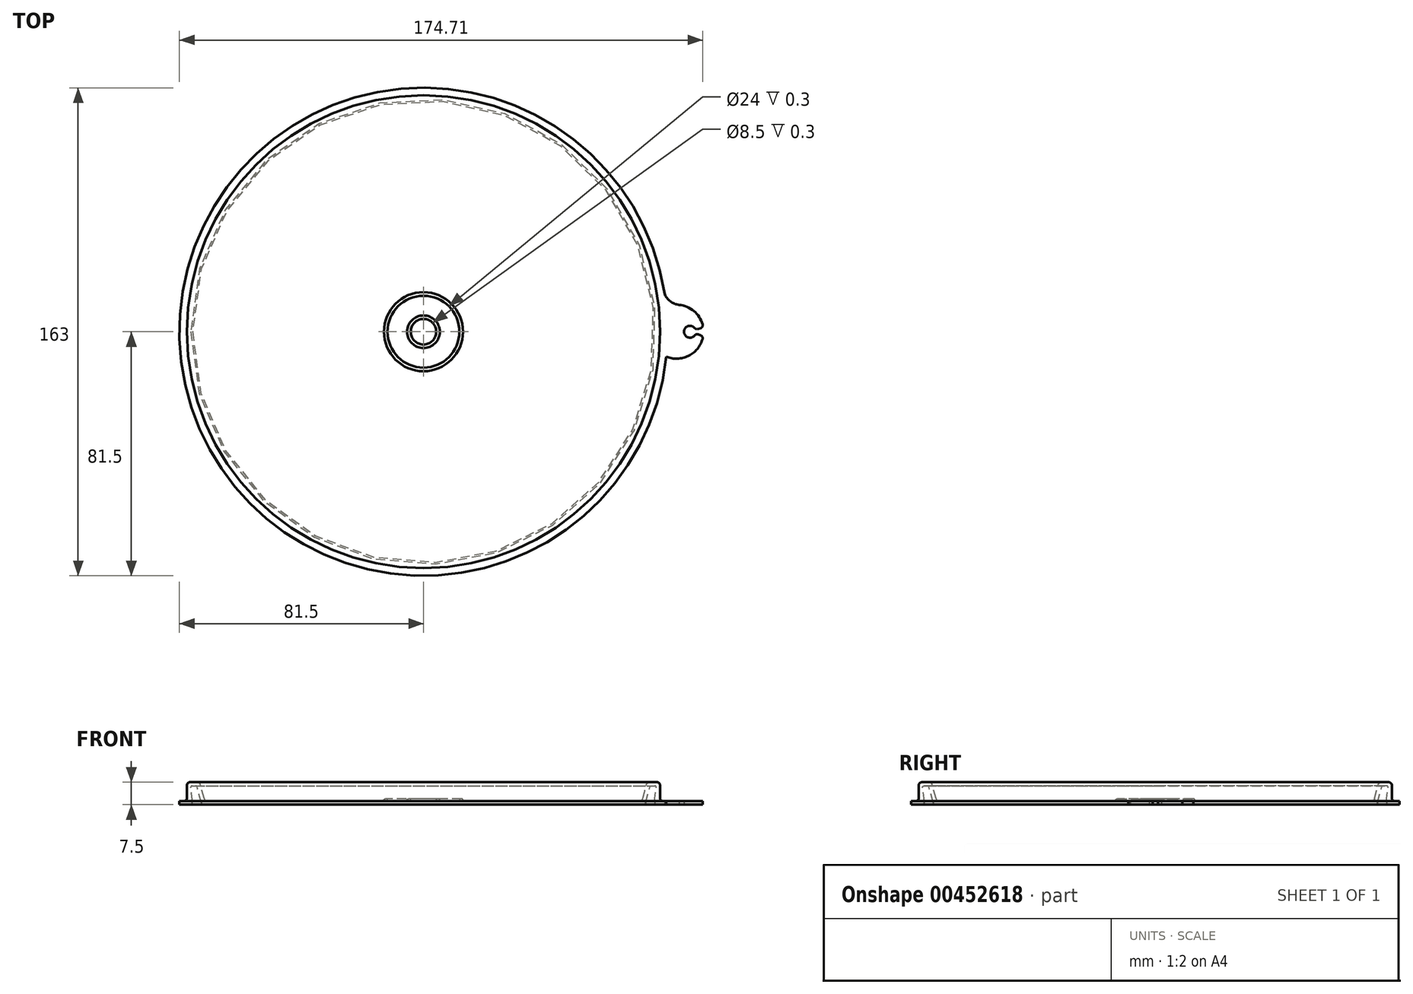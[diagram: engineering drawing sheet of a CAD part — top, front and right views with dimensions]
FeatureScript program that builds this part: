
annotation { "Feature Type Name" : "Feature", "Feature Type Description" : "" }
export const myFeature = defineFeature(function(context is Context, id is Id, definition is map)
    precondition{}
    {
        {
            var Q0;
            Q0=qCreatedBy(makeId("Top.planeOp"),FACE);
            var sketch = newSketch(context, id + "F0", { "sketchPlane" : qUnion([Q0]), "disableImprinting" : false});
            skCircle(sketch, "E0", {"center": v(0, 0) * mm, "radius": 73 * mm});
            skPoint(sketch, "E1", {"position": v(73, 0) * mm});
            skCircle(sketch, "E2", {"center": v(0, 0) * mm, "radius": 78 * mm, "construction": true});
            skLineSegment(sketch, "E3", {"start": v(0, 0) * mm, "end": v(76.56, 0) * mm, "construction": true});
            skSolve(sketch);
        }
        {
            var Q0;
            Q0 = qSketchRegion(id + "F0", true);
            extrude(context, id + "F1", {"entities" : qUnion([Q0]), "depth" : 1.2 * mm});
        }
        {
            var Q0;
            Q0=qCreatedBy(makeId("Front.planeOp"),FACE);
            var sketch = newSketch(context, id + "F2", { "sketchPlane" : qUnion([Q0]), "disableImprinting" : false});
            skLineSegment(sketch, "E4", {"start": v(73, 0) * mm, "end": v(73.23, 0) * mm});
            skLineSegment(sketch, "E5", {"start": v(74.2, 0.74) * mm, "end": v(75.59, 5.93) * mm});
            skLineSegment(sketch, "E6", {"start": v(76.07, 6.3) * mm, "end": v(77.2, 6.3) * mm});
            skLineSegment(sketch, "E7", {"start": v(77.7, 5.74) * mm, "end": v(77.14, 1.12) * mm});
            skLineSegment(sketch, "E8", {"start": v(78.13, 0) * mm, "end": v(81.5, 0) * mm});
            skLineSegment(sketch, "E9", {"start": v(81.5, 0) * mm, "end": v(81.5, 1.2) * mm});
            skLineSegment(sketch, "E10", {"start": v(81.5, 1.2) * mm, "end": v(79.97, 1.2) * mm});
            skLineSegment(sketch, "E11", {"start": v(78.97, 2.2) * mm, "end": v(78.97, 6.5) * mm});
            skLineSegment(sketch, "E12", {"start": v(77.97, 7.5) * mm, "end": v(75.46, 7.5) * mm});
            skLineSegment(sketch, "E13", {"start": v(74.49, 6.76) * mm, "end": v(73, 1.2) * mm});
            skLineSegment(sketch, "E14", {"start": v(73, 1.2) * mm, "end": v(73, 0) * mm});
            skPoint(sketch, "E15.visualSharp", {"position": v(74.69, 7.5) * mm});
            skArc(sketch, "E15.filletArc", {"start": v(75.46, 7.5) * mm, "mid": v(74.85, 7.3) * mm, "end": v(74.49, 6.76) * mm});
            skPoint(sketch, "E16.visualSharp", {"position": v(78.97, 7.5) * mm});
            skArc(sketch, "E16.filletArc", {"start": v(78.97, 6.5) * mm, "mid": v(78.68, 7.2) * mm, "end": v(77.97, 7.5) * mm});
            skPoint(sketch, "E17.visualSharp", {"position": v(78.97, 1.2) * mm});
            skArc(sketch, "E17.filletArc", {"start": v(78.97, 2.2) * mm, "mid": v(79.27, 1.5) * mm, "end": v(79.97, 1.2) * mm});
            skPoint(sketch, "E18.visualSharp", {"position": v(74, 0) * mm});
            skArc(sketch, "E18.filletArc", {"start": v(73.23, 0) * mm, "mid": v(73.84, 0.2) * mm, "end": v(74.2, 0.74) * mm});
            skPoint(sketch, "E19.visualSharp", {"position": v(77, 0) * mm});
            skArc(sketch, "E19.filletArc", {"start": v(77.14, 1.12) * mm, "mid": v(77.38, 0.34) * mm, "end": v(78.13, 0) * mm});
            skPoint(sketch, "E20.visualSharp", {"position": v(75.69, 6.3) * mm});
            skArc(sketch, "E20.filletArc", {"start": v(76.07, 6.3) * mm, "mid": v(75.77, 6.2) * mm, "end": v(75.59, 5.93) * mm});
            skPoint(sketch, "E21.visualSharp", {"position": v(77.77, 6.3) * mm});
            skArc(sketch, "E21.filletArc", {"start": v(77.7, 5.74) * mm, "mid": v(77.58, 6.13) * mm, "end": v(77.2, 6.3) * mm});
            skLineSegment(sketch, "E22", {"start": v(0, -3.65) * mm, "end": v(0, 8.92) * mm, "construction": true});
            skSolve(sketch);
        }
        {
            var Q0;
            Q0 = qSketchRegion(id + "F2", true);
            var Q1;
            Q1=sQuery(id+"F2.wireOp",EDGE,"E22");
            revolve(context, id + "F3", {"operationType" : NewBodyOperationType.ADD, "entities" : qUnion([Q0]), "axis" : qUnion([Q1]), "revolveType" : RevolveType.FULL});
        }
        {
            var Q0;
            Q0=makeQuery(id+"F1.opExtrude","CAP_FACE",FACE,{"disambiguationData":[OSD([sQuery(id+"F0.wireOp",EDGE,"E0")])],"isStart":false});
            fillet(context, id + "F4", {"entities" : qUnion([Q0]), "radius" : 1 * mm, "tangentPropagation" : true, "allowEdgeOverflow" : false});
        }
        {
            var Q0;
            Q0=qCreatedBy(makeId("Top.planeOp"),FACE);
            var sketch = newSketch(context, id + "F5", { "sketchPlane" : qUnion([Q0])});
            skCircle(sketch, "E23", {"center": v(89, 0) * mm, "radius": 2 * mm});
            skCircle(sketch, "E24", {"center": v(84.5, 0) * mm, "radius": 9 * mm});
            skCircle(sketch, "E25", {"center": v(0, 0) * mm, "radius": 81.5 * mm});
            skArc(sketch, "E26", {"start": v(80.5, 12.73) * mm, "mid": v(82.39, 10.18) * mm, "end": v(85.32, 8.96) * mm});
            skLineSegment(sketch, "E27", {"start": v(129.8, 0) * mm, "end": v(58.55, 0) * mm, "construction": true});
            skArc(sketch, "E28.MirrorCS", {"start": v(80.5, -12.73) * mm, "mid": v(82.39, -10.18) * mm, "end": v(85.32, -8.96) * mm});
            skLineSegment(sketch, "E29", {"start": v(89, 0) * mm, "end": v(94.18, 1.75) * mm});
            skLineSegment(sketch, "E30", {"start": v(94.18, 1.75) * mm, "end": v(94.18, -1.75) * mm});
            skLineSegment(sketch, "E31", {"start": v(94.18, -1.75) * mm, "end": v(89, 0) * mm});
            skPoint(sketch, "E32", {"position": v(94.18, 0) * mm});
            skSolve(sketch);
        }
        {
            var Q0;
            {var subQ4=sQuery(id+"F5.wireOp",EDGE,"E29");var subQ8=sQuery(id+"F5.wireOp",EDGE,"E23");var subQ9=makeQuery(id+"F5.imprint","INTERSECT",VERTEX,{"derivedFrom":[subQ8,subQ4]});Q0=makeQuery(id+"F5.imprint","IMPRINT",FACE,{"disambiguationData":[TD([[makeQuery(id+"F5.imprint","IMPRINT",EDGE,{"disambiguationData":[TD([[subQ9,-1.0]])],"derivedFrom":subQ8}),-1.0]])]});}
            var Q1;
            {var subQ0=sQuery(id+"F5.wireOp",EDGE,"E28.MirrorCS");Q1=makeQuery(id+"F5.imprint","IMPRINT",FACE,{"disambiguationData":[TD([[makeQuery(id+"F5.imprint","IMPRINT",EDGE,{"derivedFrom":subQ0}),1.0]])]});}
            var Q2;
            {var subQ0=sQuery(id+"F5.wireOp",EDGE,"E26");Q2=makeQuery(id+"F5.imprint","IMPRINT",FACE,{"disambiguationData":[TD([[makeQuery(id+"F5.imprint","IMPRINT",EDGE,{"derivedFrom":subQ0}),-1.0]])]});}
            extrude(context, id + "F6", {"entities" : qUnion([Q0, Q1, Q2]), "operationType" : NewBodyOperationType.ADD, "depth" : 1.2 * mm});
        }
        {
            var Q0;
            Q0=makeQuery(id+"F6.opExtrude","SWEPT_EDGE",EDGE,{"disambiguationData":[OSD([sQuery(id+"F5.wireOp",EDGE,"E24"),sQuery(id+"F5.wireOp",EDGE,"E29")])]});
            var Q1;
            Q1=makeQuery(id+"F6.opExtrude","SWEPT_EDGE",EDGE,{"disambiguationData":[OSD([sQuery(id+"F5.wireOp",EDGE,"E24"),sQuery(id+"F5.wireOp",EDGE,"E31")])]});
            var Q2;
            Q2=makeQuery(id+"F6.opExtrude","SWEPT_EDGE",EDGE,{"disambiguationData":[OSD([sQuery(id+"F5.wireOp",EDGE,"E23"),sQuery(id+"F5.wireOp",EDGE,"E29")])]});
            var Q3;
            Q3=makeQuery(id+"F6.opExtrude","SWEPT_EDGE",EDGE,{"disambiguationData":[OSD([sQuery(id+"F5.wireOp",EDGE,"E23"),sQuery(id+"F5.wireOp",EDGE,"E31")])]});
            fillet(context, id + "F7", {"entities" : qUnion([Q0, Q1, Q2, Q3]), "radius" : 1 * mm, "tangentPropagation" : true, "allowEdgeOverflow" : false});
        }
        {
            var Q0;
            Q0=makeQuery(id+"F1.opExtrude","CAP_FACE",FACE,{"disambiguationData":[OSD([sQuery(id+"F0.wireOp",EDGE,"E0")])],"isStart":false});
            var sketch = newSketch(context, id + "F8", { "sketchPlane" : qUnion([Q0])});
            skCircle(sketch, "E33", {"center": v(0, 0) * mm, "radius": 4.25 * mm});
            skCircle(sketch, "E34", {"center": v(0, 0) * mm, "radius": 5.45 * mm});
            skCircle(sketch, "E35", {"center": v(0, 0) * mm, "radius": 12 * mm});
            skCircle(sketch, "E36", {"center": v(0, 0) * mm, "radius": 13.2 * mm});
            skSolve(sketch);
        }
        {
            var Q0;
            Q0=makeQuery(id+"F8.imprint","IMPRINT",FACE,{"disambiguationData":[TD([[makeQuery(id+"F8.imprint","IMPRINT",EDGE,{"derivedFrom":sQuery(id+"F8.wireOp",EDGE,"E33")}),-1.0]])]});
            var Q1;
            Q1=makeQuery(id+"F8.imprint","IMPRINT",FACE,{"disambiguationData":[TD([[makeQuery(id+"F8.imprint","IMPRINT",EDGE,{"derivedFrom":sQuery(id+"F8.wireOp",EDGE,"E35")}),-1.0]])]});
            extrude(context, id + "F9", {"entities" : qUnion([Q0, Q1]), "operationType" : NewBodyOperationType.ADD, "depth" : 0.8 * mm});
        }
        {
            var Q0;
            Q0=makeQuery(id+"F9.opExtrude","CAP_EDGE",EDGE,{"disambiguationData":[OSD([sQuery(id+"F8.wireOp",EDGE,"E36")])],"isStart":false});
            var Q1;
            Q1=makeQuery(id+"F9.opExtrude","CAP_EDGE",EDGE,{"disambiguationData":[OSD([sQuery(id+"F8.wireOp",EDGE,"E34")])],"isStart":false});
            var Q2;
            Q2=makeQuery(id+"F9.opExtrude","CAP_EDGE",EDGE,{"disambiguationData":[OSD([sQuery(id+"F8.wireOp",EDGE,"E35")])],"isStart":false});
            var Q3;
            Q3=makeQuery(id+"F9.opExtrude","CAP_EDGE",EDGE,{"disambiguationData":[OSD([sQuery(id+"F8.wireOp",EDGE,"E33")])],"isStart":false});
            fillet(context, id + "F10", {"entities" : qUnion([Q0, Q1, Q2, Q3]), "radius" : .5 * mm, "tangentPropagation" : true, "allowEdgeOverflow" : false});
        }
    });
